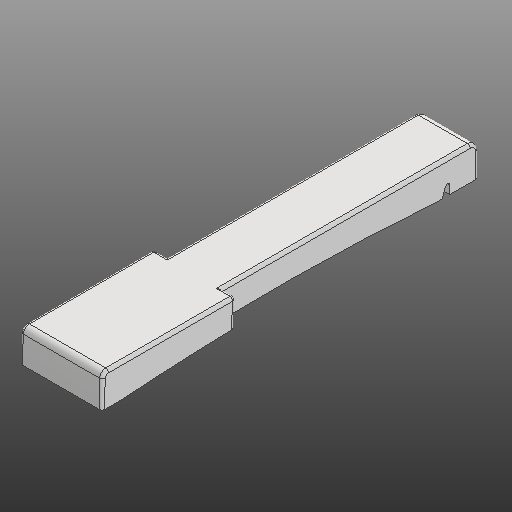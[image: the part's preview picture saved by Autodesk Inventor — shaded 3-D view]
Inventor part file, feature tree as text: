
AUTODESK INVENTOR PART (.ipt)
format: ipt  version: 2020 (Build 240168000, 168)  size: 318,464 bytes
history: native  units: in
note: dims shown in document units (in); Inventor stores cm internally (conversion verified against a paired STEP export)
features: extrude x4, other x3, fillet x2
ambient origin geometry x8: Origin, YZ Plane, XZ Plane, XY Plane, X Axis, Y Axis, Z Axis, Center Point
bodies: Solid1 (feature_tree)
feature tree (9):
  other  "Slot Start Plane"
  other  "Key Profile"
  extrude  "Upper"  TaperAngle=0.0deg  [1 undecoded]
  extrude  "Lower"  TaperAngle=0.0deg  [1 undecoded]
  extrude  "Protrusion Cutout"  Depth=0.0591in
  fillet  "Front Fillet"  Radius=0.1374in
  extrude  "Slot"  [1 undecoded]
  fillet  "Edge Softening"  Radius=0.0787in
  other  "Slot Sketch"
note: 3 required parameter values undecoded (feature->parameter linkage not recoverable at this tier; creation-order binding heuristic only, values carry confidence <= 0.55)
